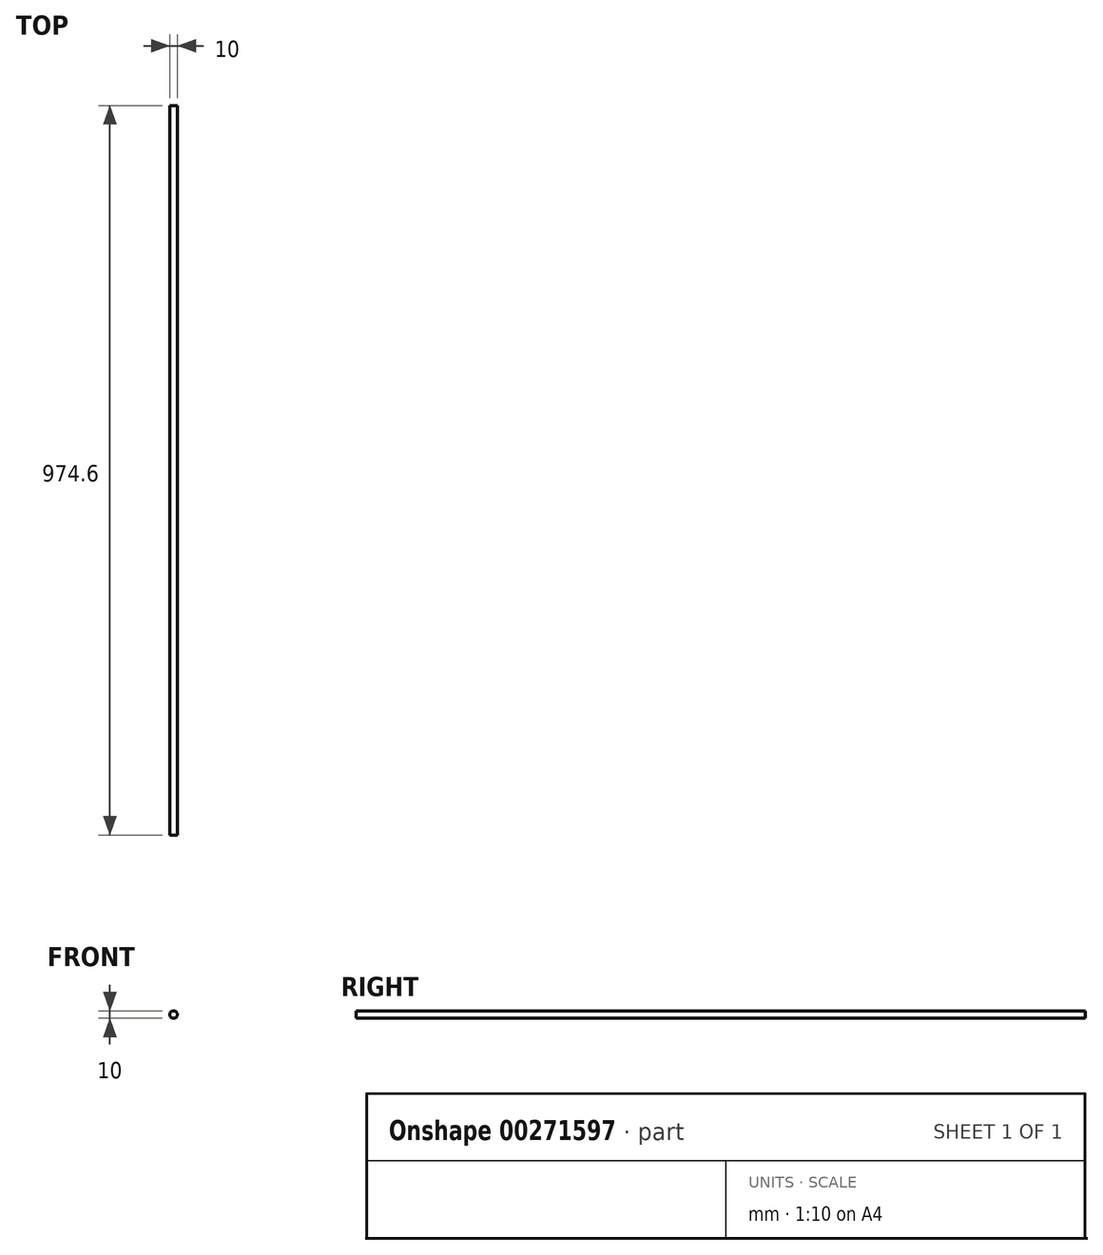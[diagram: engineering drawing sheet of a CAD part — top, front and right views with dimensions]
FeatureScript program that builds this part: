
annotation { "Feature Type Name" : "Feature", "Feature Type Description" : "" }
export const myFeature = defineFeature(function(context is Context, id is Id, definition is map)
    precondition{}
    {
        {
            var Q0;
            Q0=qCreatedBy(makeId("Front.planeOp"),FACE);
            var sketch = newSketch(context, id + "F0", { "sketchPlane" : qUnion([Q0])});
            skCircle(sketch, "E0", {"center": v(0, 0) * mm, "radius": 5 * mm});
            skSolve(sketch);
        }
        {
            var Q0;
            Q0=makeQuery(id+"F0.imprint","IMPRINT",FACE,{"disambiguationData":[TD([[makeQuery(id+"F0.imprint","IMPRINT",EDGE,{"derivedFrom":sQuery(id+"F0.wireOp",EDGE,"E0")}),1.0]])]});
            extrude(context, id + "F1", {"entities" : qUnion([Q0]), "depth" : 974.6 * mm});
        }
    });
